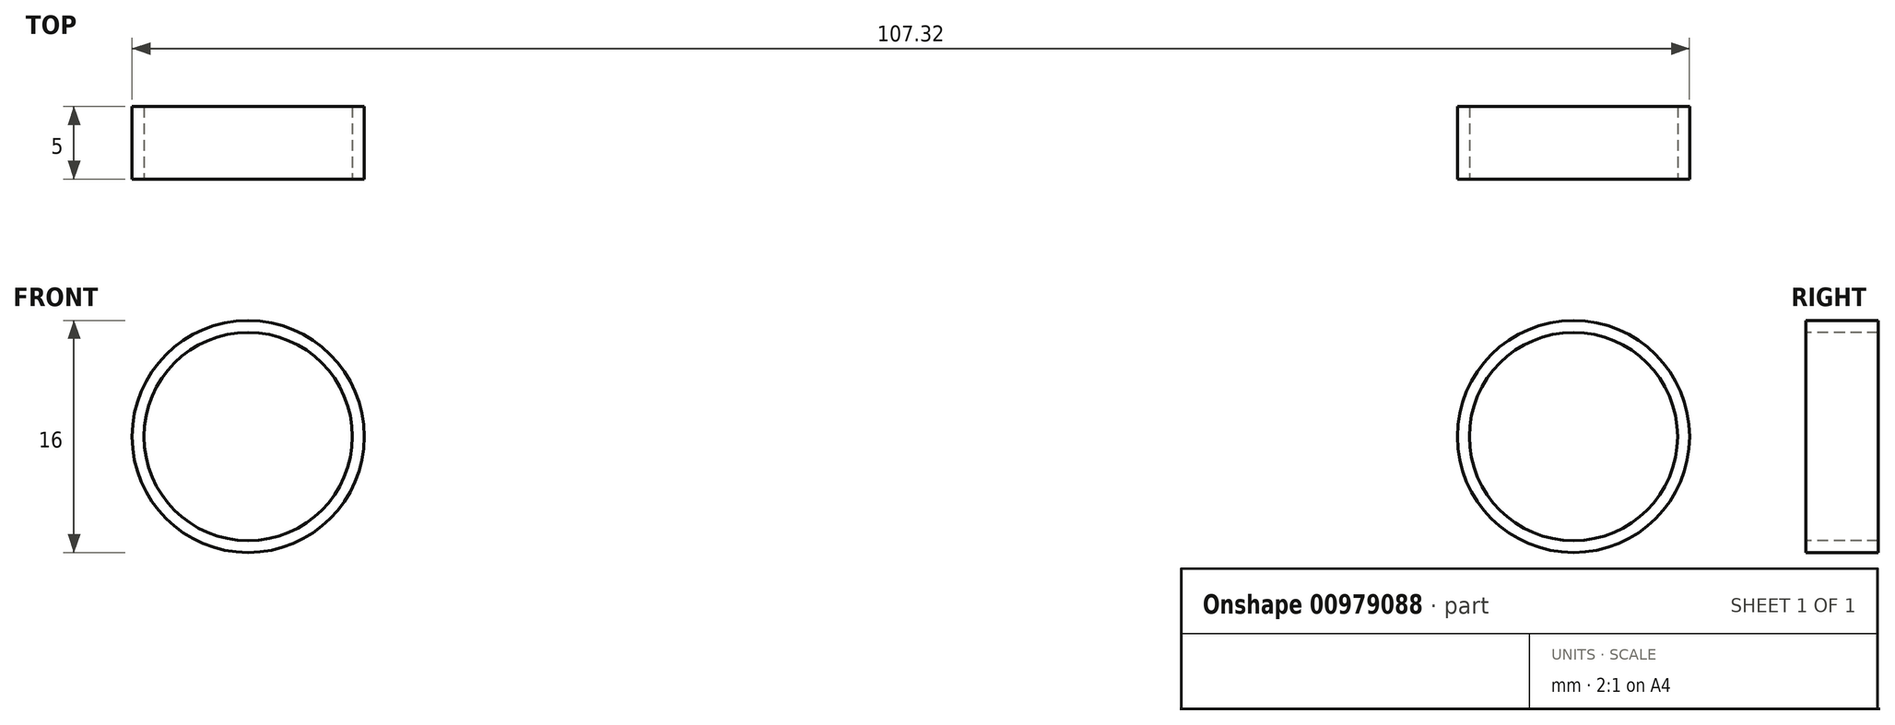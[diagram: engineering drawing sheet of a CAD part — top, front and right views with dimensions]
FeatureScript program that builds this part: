
annotation { "Feature Type Name" : "Feature", "Feature Type Description" : "" }
export const myFeature = defineFeature(function(context is Context, id is Id, definition is map)
    precondition{}
    {
        {
            var Q0;
            Q0=qCreatedBy(makeId("Front.planeOp"),FACE);
            var sketch = newSketch(context, id + "F0", { "sketchPlane" : qUnion([Q0])});
            skCircle(sketch, "E0", {"center": v(-45.66, 0) * mm, "radius": 7.17 * mm});
            skCircle(sketch, "E1", {"center": v(-45.66, 0) * mm, "radius": 8 * mm});
            skCircle(sketch, "E2.MirrorC", {"center": v(45.66, 0) * mm, "radius": 7.17 * mm});
            skCircle(sketch, "E3.MirrorC", {"center": v(45.66, 0) * mm, "radius": 8 * mm});
            skSolve(sketch);
        }
        {
            var Q0;
            Q0=sQuery(id+"F0.wireOp",EDGE,"E0");
            var Q1;
            Q1=sQuery(id+"F0.wireOp",EDGE,"E1");
            var Q2;
            Q2=sQuery(id+"F0.wireOp",EDGE,"E2.MirrorC");
            var Q3;
            Q3=sQuery(id+"F0.wireOp",EDGE,"E3.MirrorC");
            extrude(context, id + "F1", {"bodyType" : ToolBodyType.SURFACE, "surfaceEntities" : qUnion([Q0, Q1, Q2, Q3]), "depth" : 5 * mm, "offsetDistance" : 25 * mm});
        }
    });
